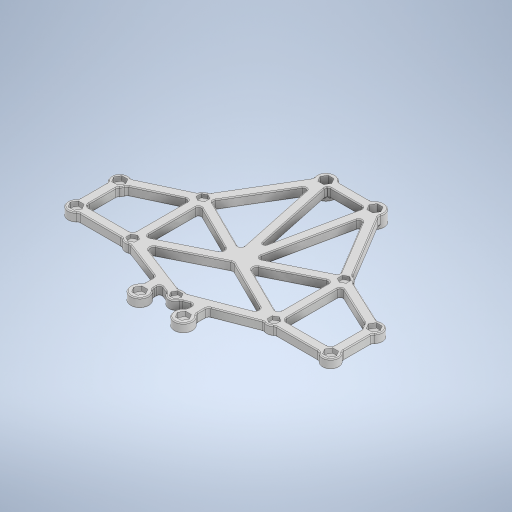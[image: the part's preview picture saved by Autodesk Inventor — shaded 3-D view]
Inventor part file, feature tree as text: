
AUTODESK INVENTOR PART (.ipt)
format: ipt  version: 2024.2 (Build 282272000, 272)  size: 1,423,360 bytes
history: native  units: mm
features: projected_geometry x67, extrude x8, sketch x6, fillet x5, hole x2
ambient origin geometry x8: Origin, YZ Plane, XZ Plane, XY Plane, X Axis, Y Axis, Z Axis, Center Point
bodies: Solid1 (feature_tree)
feature tree (88):
  sketch  "Sketch1"  dims[d0=4.8mm d9=5.6mm]
  extrude  "Extrusion1"  Depth=5.6mm
  sketch  "Sketch2"  dims[d10=24.0mm d11=9.0mm]
  extrude  "Extrusion2"  Depth=9.0mm
  extrude  "Extrusion3"  Depth=5.0mm
  extrude  "Extrusion4"  Depth=2.5mm
  extrude  "Extrusion5"  Depth=2.5mm
  hole  "Hole1"  [1 undecoded]
  hole  "Hole2"  [1 undecoded]
  fillet  "Fillet1"  Radius=2.5mm
  fillet  "Fillet2"  Radius=2.5mm
  fillet  "Fillet3"  Radius=5.0mm
  fillet  "Fillet7"  Radius=2.5mm
  fillet  "Fillet8"  Radius=5.0mm
  extrude  "Extrusion6"  Depth=2.5mm
  extrude  "Extrusion7"  Depth=2.5mm
  extrude  "Extrusion8"  Depth=2.5mm
  projected_geometry  "Projected Loop1"
  projected_geometry  "Projected Loop2"
  projected_geometry  "Projected Loop3"
  projected_geometry  "Projected Loop4"
  projected_geometry  "Projected Loop5"
  projected_geometry  "Projected Loop6"
  projected_geometry  "Projected Loop7"
  projected_geometry  "Projected Loop8"
  projected_geometry  "Projected Loop9"
  projected_geometry  "Projected Loop10"
  projected_geometry  "Projected Loop11"
  projected_geometry  "Projected Loop12"
  projected_geometry  "Projected Loop13"
  projected_geometry  "Projected Loop14"
  projected_geometry  "Projected Loop15"
  projected_geometry  "Projected Loop16"
  projected_geometry  "Projected Loop17"
  projected_geometry  "Projected Loop18"
  projected_geometry  "Projected Loop19"
  projected_geometry  "Projected Loop20"
  projected_geometry  "Projected Loop21"
  projected_geometry  "Projected Loop22"
  projected_geometry  "Projected Loop23"
  projected_geometry  "Projected Loop24"
  projected_geometry  "Projected Loop25"
  projected_geometry  "Projected Loop26"
  projected_geometry  "Projected Loop27"
  projected_geometry  "Projected Loop28"
  projected_geometry  "Projected Loop29"
  projected_geometry  "Projected Loop30"
  projected_geometry  "Projected Loop31"
  projected_geometry  "Projected Loop32"
  projected_geometry  "Projected Loop33"
  projected_geometry  "Projected Loop34"
  projected_geometry  "Projected Loop35"
  projected_geometry  "Projected Loop36"
  projected_geometry  "Projected Loop37"
  projected_geometry  "Projected Loop38"
  projected_geometry  "Projected Loop39"
  projected_geometry  "Projected Loop40"
  projected_geometry  "Projected Loop41"
  projected_geometry  "Projected Loop42"
  projected_geometry  "Projected Loop43"
  projected_geometry  "Projected Loop44"
  projected_geometry  "Projected Loop45"
  projected_geometry  "Projected Loop46"
  projected_geometry  "Projected Loop47"
  projected_geometry  "Projected Loop48"
  projected_geometry  "Projected Loop49"
  projected_geometry  "Projected Loop50"
  projected_geometry  "Projected Loop51"
  projected_geometry  "Projected Loop52"
  projected_geometry  "Projected Loop53"
  projected_geometry  "Projected Loop54"
  projected_geometry  "Projected Loop55"
  projected_geometry  "Projected Loop56"
  projected_geometry  "Projected Loop57"
  projected_geometry  "Projected Loop58"
  projected_geometry  "Projected Loop59"
  projected_geometry  "Projected Loop60"
  projected_geometry  "Projected Loop61"
  projected_geometry  "Projected Loop62"
  projected_geometry  "Projected Loop63"
  projected_geometry  "Projected Loop64"
  projected_geometry  "Projected Loop65"
  projected_geometry  "Projected Loop66"
  projected_geometry  "Projected Loop67"
  sketch  "Sketch3"  dims[d16=140.0mm d17=5.0mm]
  sketch  "Sketch4"  dims[d18=2.5mm d22=5.0mm]
  sketch  "Sketch6"  dims[d23=2.5mm d24=2.5mm]
  sketch  "Sketch7"  dims[d25=2.5mm d26=2.5mm d27=5.0mm d28=2.5mm d29=2.5mm d30=5.0mm d31=2.5mm d32=5.0mm d33=2.5mm d34=2.5mm d35=2.5mm d36=5.0mm d37=2.5mm d42=27.0mm d48=2.5mm d51=12.0mm d52=8.0mm d53=10.0mm d55=8.0mm d56=5.0mm d57=2.5mm d58=24.0mm d59=5.0mm d60=0.0mm d61=1.9mm d62=0.0mm d63=2.5mm d64=0.0mm d65=3.5mm d66=6.0mm d67=4.0mm d68=2.0mm d69=90.0deg d70=6.0mm d71=0.0mm d72=5.25mm d73=6.0mm d74=4.0mm d75=2.0mm d76=90.0deg d77=1.0mm d78=0.0mm d79=5.0mm d80=0.0mm d81=2.0mm d82=2.0mm d83=1.5mm d90=96.0mm d91=5.0mm d92=2.5mm d95=2.5mm d96=2.5mm d97=2.5mm d98=5.0mm d100=2.0mm d101=0.0mm d102=5.0mm d103=15.0mm d104=2.5mm d105=2.5mm d106=2.5mm d107=5.0mm d108=5.0mm d109=2.5mm d110=42.0mm d127=73.0mm d129=0.2mm d130=0.0mm d131=0.2mm d132=0.0mm d133=0.2mm d134=0.0mm d135=5.0mm d136=2.5mm d137=5.0mm d138=2.5mm d139=8.0mm d140=1.0mm d141=0.5mm d142=70.0mm d84=0.0mm d85=0.0mm d86=0.0mm d87=0.0mm]
note: 2 required parameter values undecoded (feature->parameter linkage not recoverable at this tier; creation-order binding heuristic only, values carry confidence <= 0.55)
